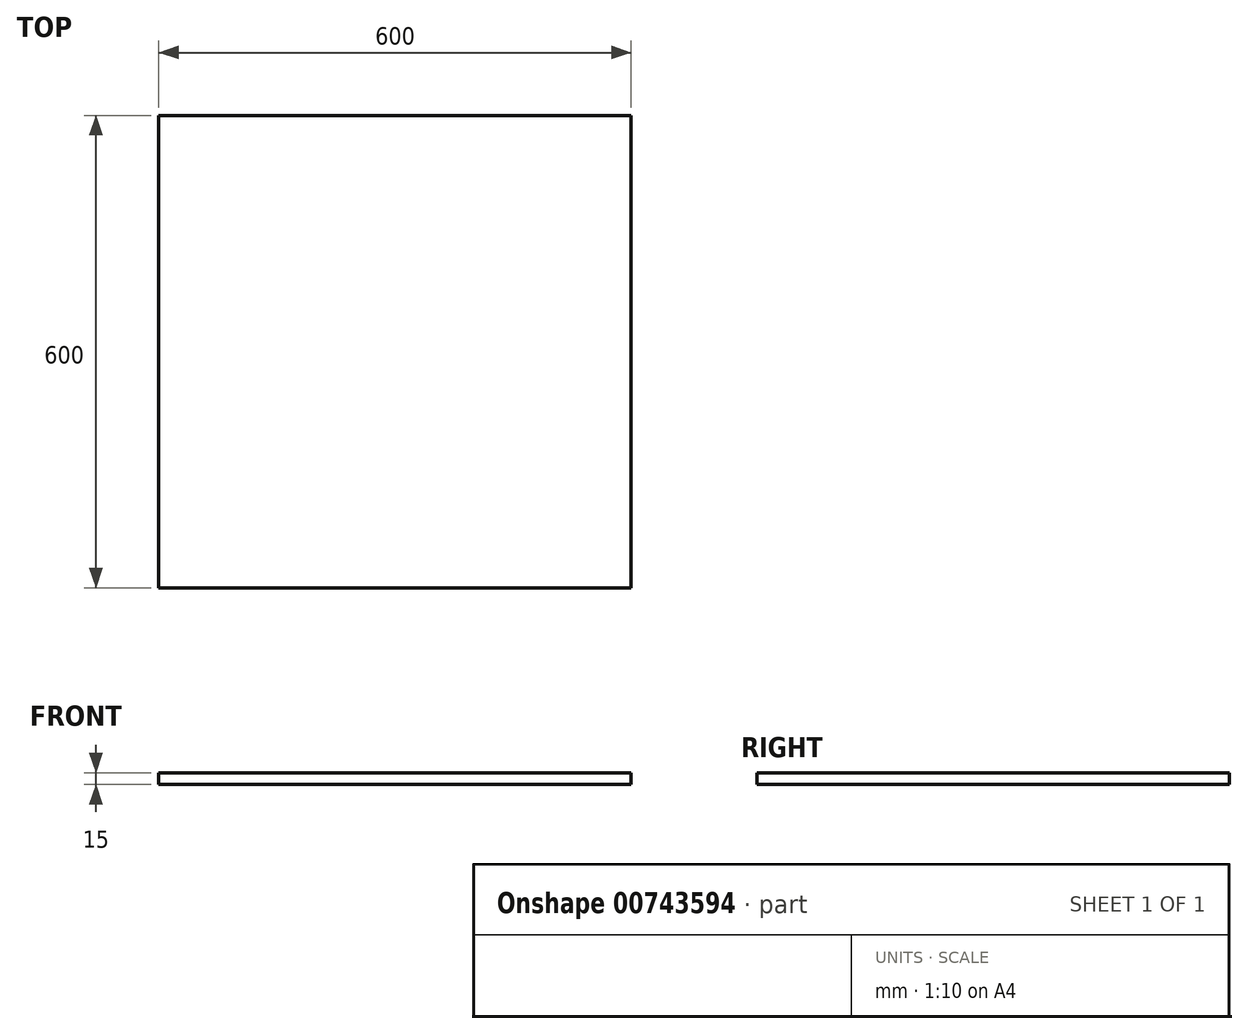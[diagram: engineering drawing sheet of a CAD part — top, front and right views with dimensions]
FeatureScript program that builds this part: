
annotation { "Feature Type Name" : "Feature", "Feature Type Description" : "" }
export const myFeature = defineFeature(function(context is Context, id is Id, definition is map)
    precondition{}
    {
        {
            var Q0;
            Q0=qCreatedBy(makeId("Top.planeOp"),FACE);
            var sketch = newSketch(context, id + "F0", { "sketchPlane" : qUnion([Q0])});
            skLineSegment(sketch, "E0.bottom", {"start": v(300, -300) * mm, "end": v(-300, -300) * mm});
            skLineSegment(sketch, "E0.top", {"start": v(300, 300) * mm, "end": v(-300, 300) * mm});
            skLineSegment(sketch, "E0.left", {"start": v(300, -300) * mm, "end": v(300, 300) * mm});
            skLineSegment(sketch, "E0.right", {"start": v(-300, -300) * mm, "end": v(-300, 300) * mm});
            skPoint(sketch, "E0.middle", {"position": v(0, 0) * mm});
            skSolve(sketch);
        }
        {
            var Q0;
            Q0 = qSketchRegion(id + "F0", true);
            extrude(context, id + "F1", {"entities" : qUnion([Q0]), "depth" : 15 * mm, "offsetDistance" : 25 * mm});
        }
    });
